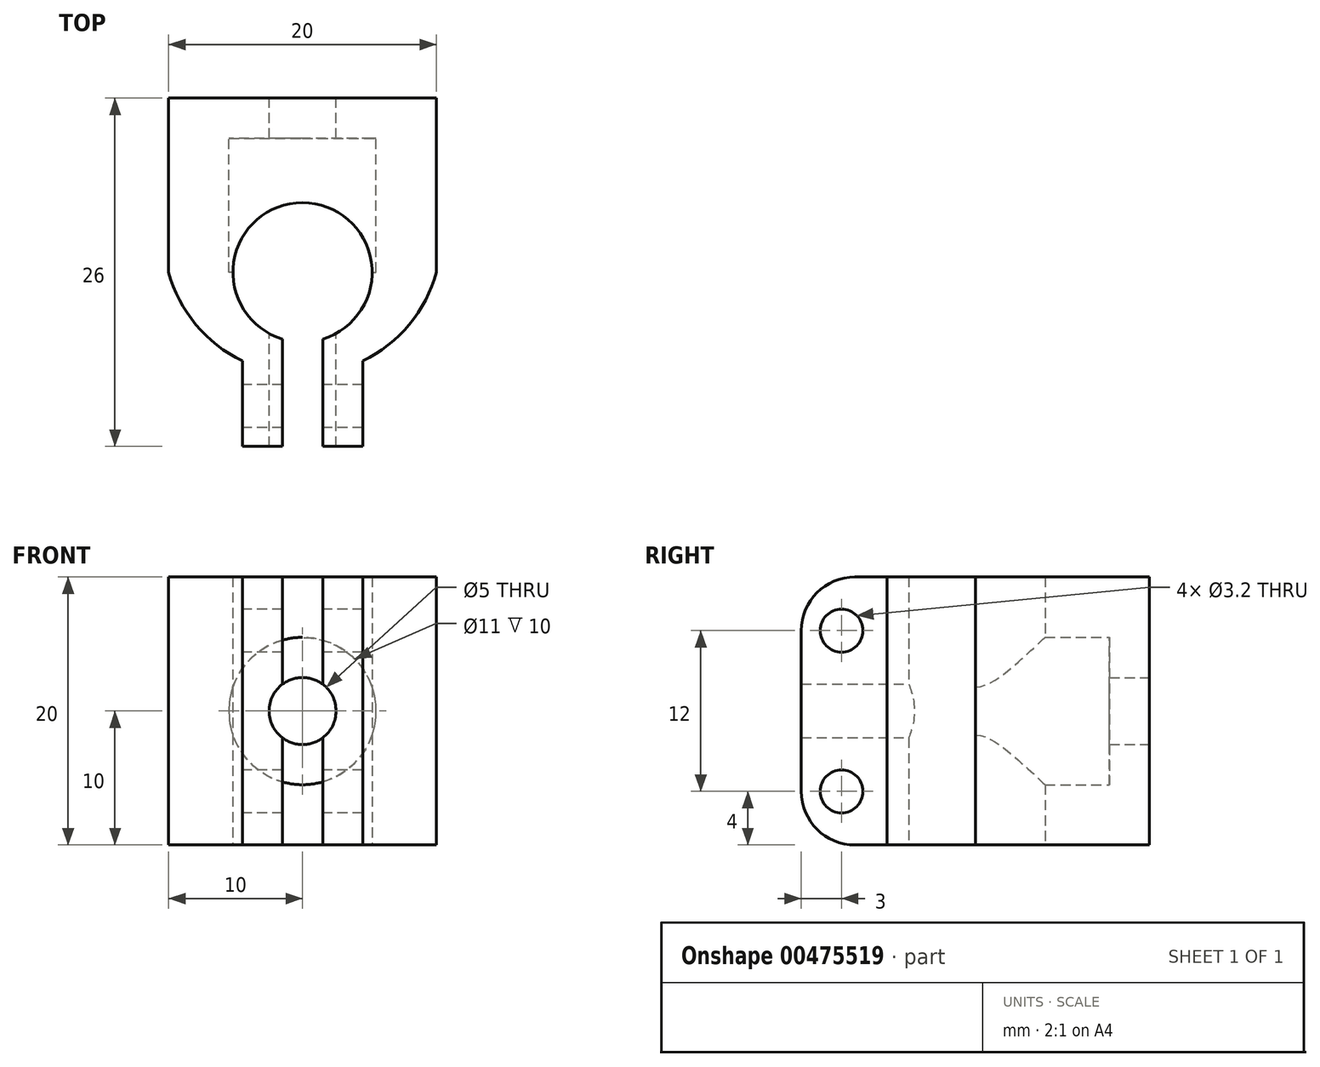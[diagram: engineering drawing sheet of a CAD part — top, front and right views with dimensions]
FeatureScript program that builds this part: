
annotation { "Feature Type Name" : "Feature", "Feature Type Description" : "" }
export const myFeature = defineFeature(function(context is Context, id is Id, definition is map)
    precondition{}
    {
        {
            var Q0;
            Q0=qCreatedBy(makeId("Top.planeOp"),FACE);
            var sketch = newSketch(context, id + "F0", { "sketchPlane" : qUnion([Q0])});
            skLineSegment(sketch, "E0.bottom", {"start": v(-10, 13) * mm, "end": v(10, 13) * mm});
            skLineSegment(sketch, "E0.top", {"start": v(-10, -13) * mm, "end": v(10, -13) * mm});
            skLineSegment(sketch, "E0.left", {"start": v(-10, 13) * mm, "end": v(-10, -13) * mm});
            skLineSegment(sketch, "E0.right", {"start": v(10, 13) * mm, "end": v(10, -13) * mm});
            skPoint(sketch, "E0.middle", {"position": v(0, 0) * mm});
            skCircle(sketch, "E1", {"center": v(0, 0) * mm, "radius": 5.2 * mm});
            skLineSegment(sketch, "E2", {"start": v(-1.5, -13) * mm, "end": v(-1.5, -4.98) * mm});
            skLineSegment(sketch, "E3.MirrorCS", {"start": v(1.5, -13) * mm, "end": v(1.5, -4.98) * mm});
            skCircle(sketch, "E4", {"center": v(0, 0) * mm, "radius": 8 * mm, "construction": true});
            skLineSegment(sketch, "E5", {"start": v(-4.5, -13) * mm, "end": v(-4.5, -6.61) * mm});
            skLineSegment(sketch, "E6.MirrorCS", {"start": v(4.5, -13) * mm, "end": v(4.5, -6.61) * mm});
            skArc(sketch, "E7", {"start": v(-10, 0) * mm, "mid": v(-7.97, -3.9) * mm, "end": v(-4.5, -6.61) * mm});
            skArc(sketch, "E8.MirrorCS", {"start": v(10, 0) * mm, "mid": v(7.97, -3.9) * mm, "end": v(4.5, -6.61) * mm});
            skSolve(sketch);
        }
        {
            var Q0;
            Q0=makeQuery(id+"F0.imprint","IMPRINT",FACE,{"disambiguationData":[TD([[makeQuery(id+"F0.imprint","IMPRINT",EDGE,{"derivedFrom":sQuery(id+"F0.wireOp",EDGE,"E0.bottom")}),-1.0]])]});
            extrude(context, id + "F1", {"entities" : qUnion([Q0]), "endBound" : BoundingType.SYMMETRIC, "depth" : 20 * mm});
        }
        {
            var Q0;
            Q0=makeQuery(id+"F1.opExtrude","SWEPT_FACE",FACE,{"disambiguationData":[OSD([sQuery(id+"F0.wireOp",EDGE,"E0.bottom")])]});
            var sketch = newSketch(context, id + "F2", { "sketchPlane" : qUnion([Q0])});
            skCircle(sketch, "E9", {"center": v(0, 0) * mm, "radius": 5.5 * mm});
            skSolve(sketch);
        }
        {
            var Q0;
            Q0=sQuery(id+"F2.wireOp",VERTEX,"E9.center");
            var Q1;
            Q1=makeQuery(id+"F1.opExtrude","SWEPT_BODY",BODY,{"disambiguationData":[OSD([sQuery(id+"F0.wireOp",EDGE,"E0.bottom"),sQuery(id+"F0.wireOp",EDGE,"E0.top"),sQuery(id+"F0.wireOp",EDGE,"E0.left"),sQuery(id+"F0.wireOp",EDGE,"E0.right"),sQuery(id+"F0.wireOp",EDGE,"E1"),sQuery(id+"F0.wireOp",EDGE,"E2"),sQuery(id+"F0.wireOp",EDGE,"E3.MirrorCS")])]});
            hole(context, id + "F3", {"style" : HoleStyle.SIMPLE, "endStyle" : HoleEndStyle.THROUGH, "holeDiameter" : 5 * mm, "isTappedThrough" : true, "tappedDepth" : 12 * mm, "tapClearance" : 3, "startFromSketch" : true, "locations" : qUnion([Q0]), "scope" : qUnion([Q1])});
        }
        {
            var Q0;
            Q0=makeQuery(id+"F1.opExtrude","SWEPT_FACE",FACE,{"disambiguationData":[OSD([sQuery(id+"F0.wireOp",EDGE,"E5")])]});
            var sketch = newSketch(context, id + "F4", { "sketchPlane" : qUnion([Q0])});
            skCircle(sketch, "E10", {"center": v(10, -6) * mm, "radius": 1.6 * mm});
            skCircle(sketch, "E11.0.1.0", {"center": v(10, 6) * mm, "radius": 1.6 * mm});
            skLineSegment(sketch, "E11.direction1", {"start": v(10, -6) * mm, "end": v(35, -6) * mm, "construction": true});
            skLineSegment(sketch, "E11.direction2", {"start": v(10, -6) * mm, "end": v(10, 6) * mm, "construction": true});
            skSolve(sketch);
        }
        {
            var Q0;
            Q0=makeQuery(id+"F4.imprint","IMPRINT",FACE,{"disambiguationData":[TD([[makeQuery(id+"F4.imprint","IMPRINT",EDGE,{"derivedFrom":sQuery(id+"F4.wireOp",EDGE,"E11.0.1.0")}),1.0]])]});
            var Q1;
            Q1=makeQuery(id+"F4.imprint","IMPRINT",FACE,{"disambiguationData":[TD([[makeQuery(id+"F4.imprint","IMPRINT",EDGE,{"derivedFrom":sQuery(id+"F4.wireOp",EDGE,"E10")}),1.0]])]});
            extrude(context, id + "F5", {"entities" : qUnion([Q0, Q1]), "operationType" : NewBodyOperationType.REMOVE, "endBound" : BoundingType.THROUGH_ALL, "oppositeDirection" : true, "depth" : 25 * mm});
        }
        {
            var Q0;
            Q0=qCreatedBy(makeId("Front.planeOp"),FACE);
            cPlane(context, id + "F6", {"entities" : qUnion([Q0]), "cplaneType" : CPlaneType.OFFSET, "offset" : 10 * mm, "oppositeDirection" : true, "width" : 150 * mm, "height" : 150 * mm});
        }
        {
            var Q0;
            Q0=qCreatedBy(id+"F6.planeOp",FACE);
            var sketch = newSketch(context, id + "F7", { "sketchPlane" : qUnion([Q0])});
            skCircle(sketch, "E12", {"center": v(0, 0) * mm, "radius": 5.5 * mm});
            skSolve(sketch);
        }
        {
            var Q0;
            Q0 = qSketchRegion(id + "F7", true);
            var Q1;
            Q1=makeQuery(id+"F1.opExtrude","SWEPT_FACE",FACE,{"disambiguationData":[OSD([sQuery(id+"F0.wireOp",EDGE,"E1")])]});
            var Q2;
            Q2=qCreatedBy(makeId("Origin.pointOp"),VERTEX);
            extrude(context, id + "F8", {"entities" : qUnion([Q0]), "operationType" : NewBodyOperationType.REMOVE, "endBound" : BoundingType.UP_TO_VERTEX, "endBoundEntityFace" : qUnion([Q1]), "endBoundEntityVertex" : qUnion([Q2]), "depth" : 25 * mm});
        }
        {
            var Q0;
            {var subQ0=sQuery(id+"F0.wireOp",EDGE,"E0.top");Q0=makeQuery(id+"F1.opExtrude","CAP_EDGE",EDGE,{"disambiguationData":[OSD([subQ0]),TDD([makeQuery(id+"F0.imprint","IMPRINT",EDGE,{"disambiguationData":[TD([[makeQuery(id+"F0.imprint","INTERSECT",VERTEX,{"derivedFrom":[subQ0,sQuery(id+"F0.wireOp",EDGE,"E3.MirrorCS")]}),-1.0]])],"derivedFrom":subQ0})])],"isStart":false});}
            var Q1;
            {var subQ0=sQuery(id+"F0.wireOp",EDGE,"E0.top");Q1=makeQuery(id+"F1.opExtrude","CAP_EDGE",EDGE,{"disambiguationData":[OSD([subQ0]),TDD([makeQuery(id+"F0.imprint","IMPRINT",EDGE,{"disambiguationData":[TD([[makeQuery(id+"F0.imprint","INTERSECT",VERTEX,{"derivedFrom":[subQ0,sQuery(id+"F0.wireOp",EDGE,"E2")]}),1.0]])],"derivedFrom":subQ0})])],"isStart":false});}
            var Q2;
            {var subQ0=sQuery(id+"F0.wireOp",EDGE,"E0.top");Q2=makeQuery(id+"F1.opExtrude","CAP_EDGE",EDGE,{"disambiguationData":[OSD([subQ0]),TDD([makeQuery(id+"F0.imprint","IMPRINT",EDGE,{"disambiguationData":[TD([[makeQuery(id+"F0.imprint","INTERSECT",VERTEX,{"derivedFrom":[subQ0,sQuery(id+"F0.wireOp",EDGE,"E2")]}),1.0]])],"derivedFrom":subQ0})])],"isStart":true});}
            var Q3;
            {var subQ0=sQuery(id+"F0.wireOp",EDGE,"E0.top");Q3=makeQuery(id+"F1.opExtrude","CAP_EDGE",EDGE,{"disambiguationData":[OSD([subQ0]),TDD([makeQuery(id+"F0.imprint","IMPRINT",EDGE,{"disambiguationData":[TD([[makeQuery(id+"F0.imprint","INTERSECT",VERTEX,{"derivedFrom":[subQ0,sQuery(id+"F0.wireOp",EDGE,"E3.MirrorCS")]}),-1.0]])],"derivedFrom":subQ0})])],"isStart":true});}
            fillet(context, id + "F9", {"entities" : qUnion([Q0, Q1, Q2, Q3]), "radius" : 4 * mm, "tangentPropagation" : true, "allowEdgeOverflow" : false});
        }
    });
